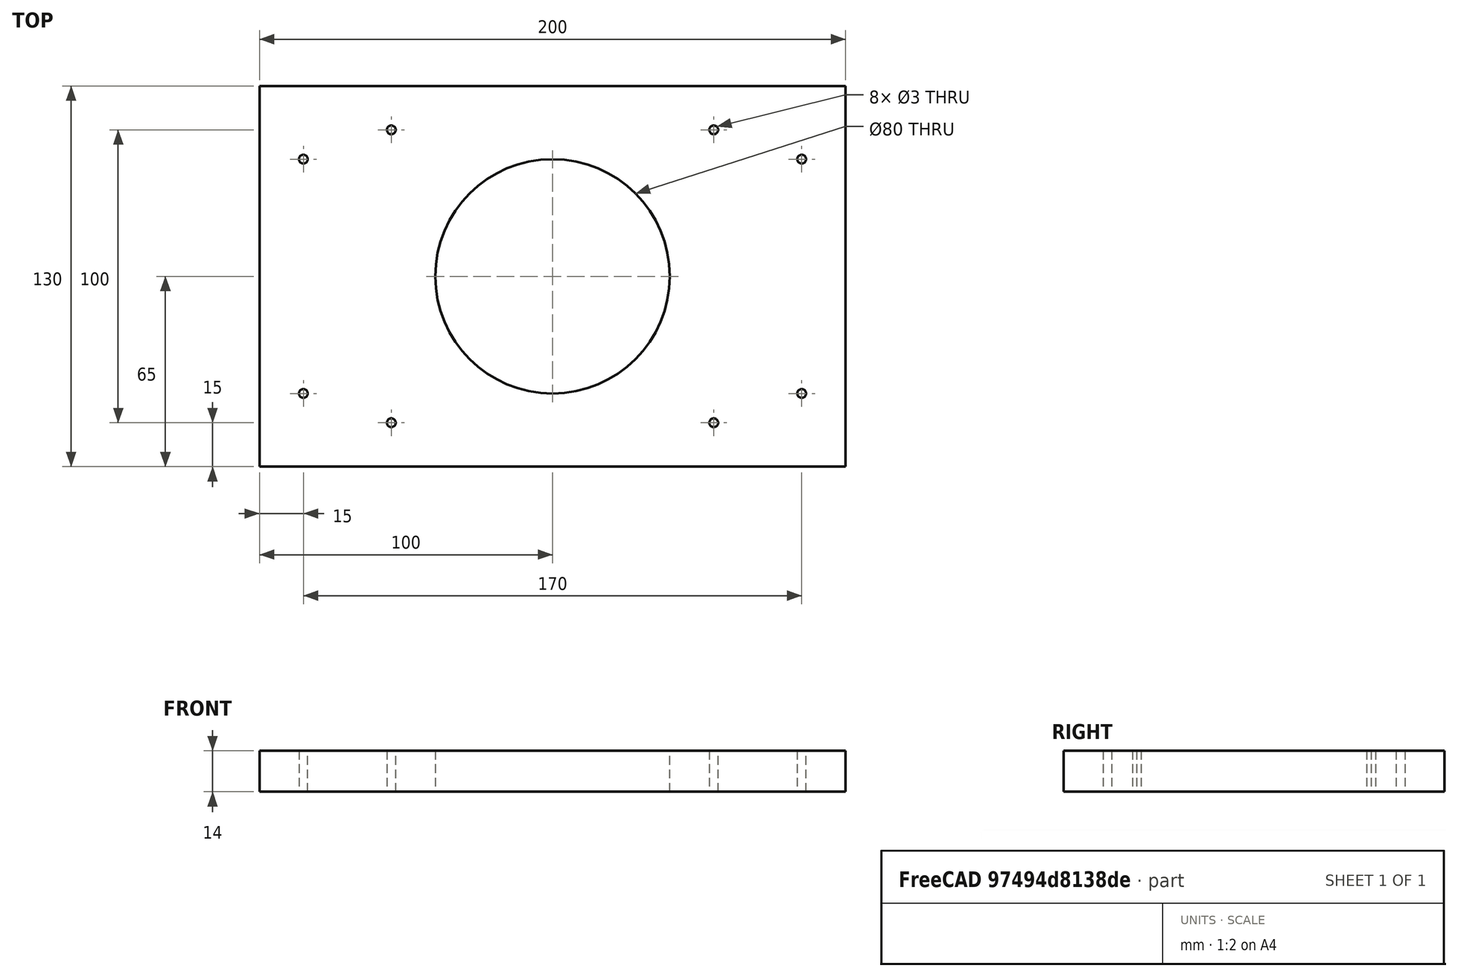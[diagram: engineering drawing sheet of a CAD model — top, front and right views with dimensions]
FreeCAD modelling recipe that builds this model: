
FCSTD DOCUMENT  (FreeCAD 0.19R24276 (Git))
Label: Plate_200x130_d80_4napravl_4_krep_otv
License: All rights reserved
LicenseURL: http://en.wikipedia.org/wiki/All_rights_reserved
objects: Sketcher::SketchObject×1, PartDesign::Pad×1, PartDesign::Body×1
note: 4 computed .brp shape members not serialized (recipe doc carries the construction recipe); baked Part::Feature solids carry a one-line shape summary decoded from their .brp

FEATURE [Sketcher::SketchObject] Sketch
  FullyConstrained = true
  MapMode = 5
  Support = -> [XY_Plane]
  sketch-geometry (21):
    g0: LineSegment StartX=0 StartY=0 StartZ=0 EndX=200 EndY=0 EndZ=0
    g1: LineSegment StartX=200 StartY=0 StartZ=0 EndX=200 EndY=130 EndZ=0
    g2: LineSegment StartX=200 StartY=130 StartZ=0 EndX=0 EndY=130 EndZ=0
    g3: LineSegment StartX=0 StartY=130 StartZ=0 EndX=0 EndY=0 EndZ=0
    g4: Circle CenterX=100 CenterY=65 CenterZ=0 NormalX=0 NormalY=0 NormalZ=1 AngleXU=0 Radius=40
    g5: Circle CenterX=45 CenterY=115 CenterZ=0 NormalX=0 NormalY=0 NormalZ=1 AngleXU=0 Radius=1.5
    g6: Circle CenterX=45 CenterY=15 CenterZ=0 NormalX=0 NormalY=0 NormalZ=1 AngleXU=0 Radius=1.5
    g7: Circle CenterX=155 CenterY=115 CenterZ=0 NormalX=0 NormalY=0 NormalZ=1 AngleXU=0 Radius=1.5
    g8: Circle CenterX=155 CenterY=15 CenterZ=0 NormalX=0 NormalY=0 NormalZ=1 AngleXU=0 Radius=1.5
    g9: LineSegment StartX=45 StartY=15 StartZ=0 EndX=45 EndY=115 EndZ=0
    g10: LineSegment StartX=45 StartY=15 StartZ=0 EndX=155 EndY=15 EndZ=0
    g11: LineSegment StartX=155 StartY=115 StartZ=0 EndX=155 EndY=15 EndZ=0
    g12: LineSegment StartX=45 StartY=115 StartZ=0 EndX=155 EndY=115 EndZ=0
    g13: Circle CenterX=15 CenterY=105 CenterZ=0 NormalX=0 NormalY=0 NormalZ=1 AngleXU=0 Radius=1.5
    g14: Circle CenterX=15 CenterY=25 CenterZ=0 NormalX=0 NormalY=0 NormalZ=1 AngleXU=0 Radius=1.5
    g15: Circle CenterX=185 CenterY=105 CenterZ=0 NormalX=0 NormalY=0 NormalZ=1 AngleXU=0 Radius=1.5
    g16: Circle CenterX=185 CenterY=25 CenterZ=0 NormalX=0 NormalY=0 NormalZ=1 AngleXU=0 Radius=1.5
    g17: LineSegment StartX=15 StartY=105 StartZ=0 EndX=15 EndY=25 EndZ=0
    g18: LineSegment StartX=185 StartY=105 StartZ=0 EndX=185 EndY=25 EndZ=0
    g19: LineSegment StartX=15 StartY=25 StartZ=0 EndX=185 EndY=25 EndZ=0
    g20: LineSegment StartX=185 StartY=105 StartZ=0 EndX=15 EndY=105 EndZ=0
  constraints (52):
    c: Coincident(g0,g1)
    c: Coincident(g1,g2)
    c: Coincident(g2,g3)
    c: Coincident(g3,g0)
    c: Horizontal(g0)
    c: Horizontal(g2)
    c: Vertical(g1)
    c: Vertical(g3)
    c: Coincident(g0,g-1)
    c: DistanceY(g1,g1) = 130
    c: DistanceX(g0,g0) = 200
    c: Symmetric(g2,g0,g4)
    c: Diameter(g4) = 80
    c: DistanceX(g0,g6) = 45
    c: Coincident(g9,g6)
    c: Coincident(g9,g5)
    c: Vertical(g9)
    c: Coincident(g10,g6)
    c: Coincident(g10,g8)
    c: Horizontal(g10)
    c: Coincident(g11,g7)
    c: Coincident(g11,g8)
    c: Vertical(g11)
    c: Coincident(g12,g5)
    c: Coincident(g12,g7)
    c: Horizontal(g12)
    c: Symmetric(g7,g6,g4)
    c: DistanceY(g0,g6) = 15
    c: Coincident(g17,g13)
    c: Coincident(g17,g14)
    c: Coincident(g18,g15)
    c: Coincident(g18,g16)
    c: Vertical(g18)
    c: Coincident(g19,g14)
    c: Coincident(g19,g16)
    c: Vertical(g17)
    c: Horizontal(g19)
    c: Coincident(g20,g15)
    c: Coincident(g20,g13)
    c: Horizontal(g20)
    c: Diameter(g5) = 3
    c: Equal(g5,g6)
    c: Equal(g5,g8)
    c: Equal(g5,g7)
    c: Diameter(g13) = 3
    c: Equal(g13,g14)
    c: Equal(g13,g15)
    c: Equal(g13,g16)
    c: DistanceY(g13,g2) = 25
    c: DistanceY(g0,g14) = 25
    c: DistanceX(g0,g14) = 15
    c: DistanceX(g16,g0) = 15
FEATURE [PartDesign::Pad] Pad
  Direction = (1,1,1)
  Length = 14
  Length2 = 100
  Profile = -> Sketch
  Type = 0
FEATURE [PartDesign::Body] Body
  Group = -> [Sketch,Pad]
  Origin = -> Origin
  Tip = -> Pad
